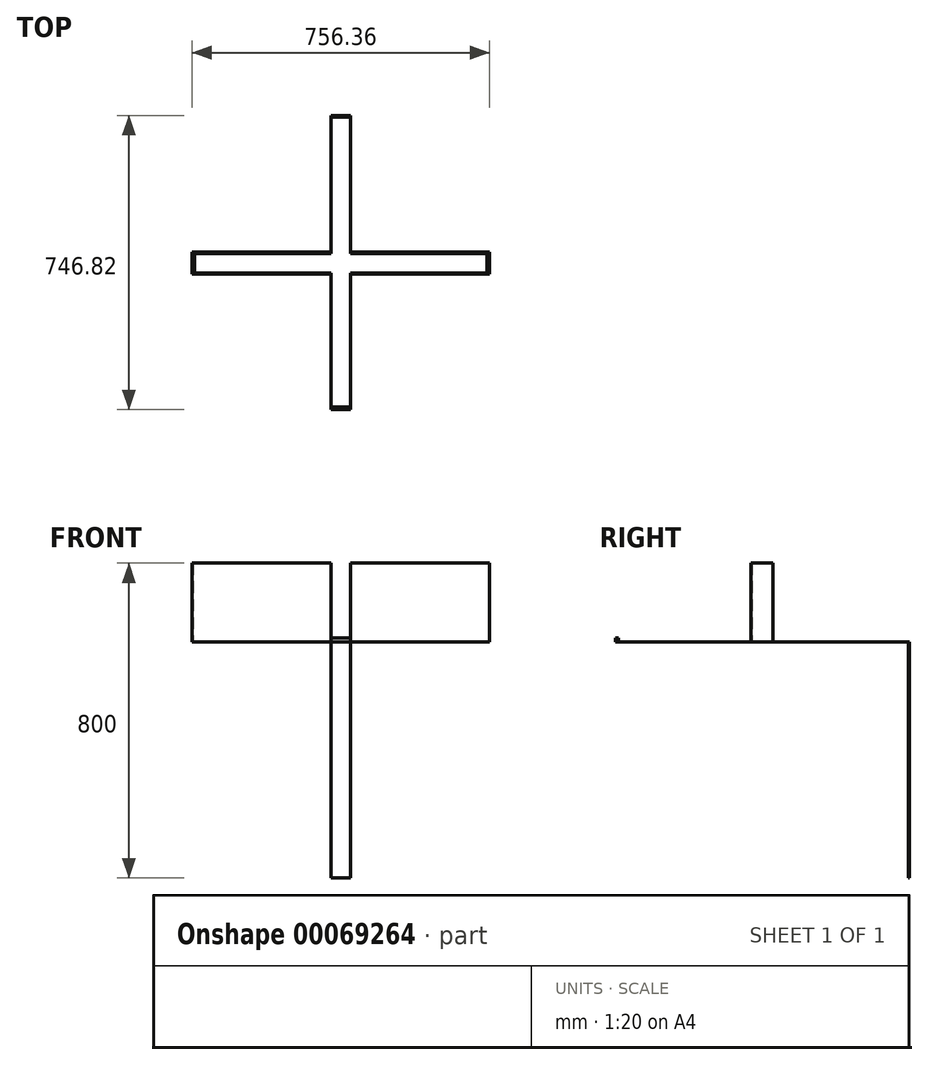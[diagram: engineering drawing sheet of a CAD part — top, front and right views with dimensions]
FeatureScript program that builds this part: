
annotation { "Feature Type Name" : "Feature", "Feature Type Description" : "" }
export const myFeature = defineFeature(function(context is Context, id is Id, definition is map)
    precondition{}
    {
        {
            var Q0;
            Q0=qCreatedBy(makeId("Top.planeOp"),FACE);
            var sketch = newSketch(context, id + "F0", { "sketchPlane" : qUnion([Q0])});
            skLineSegment(sketch, "E0.rect.bottom", {"start": v(375, 25) * mm, "end": v(-375, 25) * mm});
            skLineSegment(sketch, "E0.rect.top", {"start": v(375, -25) * mm, "end": v(-375, -25) * mm});
            skLineSegment(sketch, "E0.rect.left", {"start": v(375, 25) * mm, "end": v(375, -25) * mm});
            skLineSegment(sketch, "E0.rect.right", {"start": v(-375, 25) * mm, "end": v(-375, -25) * mm});
            skPoint(sketch, "E0.rect.middle", {"position": v(0, 0) * mm});
            skLineSegment(sketch, "E1.rect.bottom", {"start": v(-25, 375) * mm, "end": v(25, 375) * mm});
            skLineSegment(sketch, "E1.rect.top", {"start": v(-25, -375) * mm, "end": v(25, -375) * mm});
            skLineSegment(sketch, "E1.rect.left", {"start": v(-25, 375) * mm, "end": v(-25, -375) * mm});
            skLineSegment(sketch, "E1.rect.right", {"start": v(25, 375) * mm, "end": v(25, -375) * mm});
            skPoint(sketch, "E2", {"position": v(25, 25) * mm});
            skPoint(sketch, "E3", {"position": v(-25, 25) * mm});
            skPoint(sketch, "E4", {"position": v(-25, -25) * mm});
            skPoint(sketch, "E5", {"position": v(25, -25) * mm});
            skLineSegment(sketch, "E6", {"start": v(-25, -365) * mm, "end": v(25, -365) * mm});
            skLineSegment(sketch, "E7", {"start": v(25, -28.18) * mm, "end": v(378.18, -28.18) * mm});
            skLineSegment(sketch, "E8", {"start": v(378.18, -28.18) * mm, "end": v(378.18, 28.18) * mm});
            skLineSegment(sketch, "E9", {"start": v(378.18, 28.18) * mm, "end": v(25, 28.18) * mm});
            skLineSegment(sketch, "E10", {"start": v(-25, 28.18) * mm, "end": v(-378.18, 28.18) * mm});
            skLineSegment(sketch, "E11", {"start": v(-378.18, 28.18) * mm, "end": v(-378.18, -28.18) * mm});
            skLineSegment(sketch, "E12", {"start": v(-378.18, -28.18) * mm, "end": v(-25, -28.18) * mm});
            skLineSegment(sketch, "E13.bottom", {"start": v(375, 25) * mm, "end": v(371.83, 25) * mm});
            skLineSegment(sketch, "E13.top", {"start": v(375, -25) * mm, "end": v(371.83, -25) * mm});
            skLineSegment(sketch, "E13.right", {"start": v(371.83, 25) * mm, "end": v(371.83, -25) * mm});
            skLineSegment(sketch, "E14.bottom", {"start": v(25, -375) * mm, "end": v(-25, -375) * mm});
            skLineSegment(sketch, "E14.top", {"start": v(25, -371.83) * mm, "end": v(-25, -371.83) * mm});
            skLineSegment(sketch, "E14.left", {"start": v(25, -375) * mm, "end": v(25, -371.83) * mm});
            skLineSegment(sketch, "E14.right", {"start": v(-25, -375) * mm, "end": v(-25, -371.83) * mm});
            skLineSegment(sketch, "E15.bottom", {"start": v(-375, 25) * mm, "end": v(-371.83, 25) * mm});
            skLineSegment(sketch, "E15.top", {"start": v(-375, -25) * mm, "end": v(-371.83, -25) * mm});
            skLineSegment(sketch, "E15.right", {"start": v(-371.83, 25) * mm, "end": v(-371.83, -25) * mm});
            skLineSegment(sketch, "E16.top", {"start": v(-25, 371.83) * mm, "end": v(25, 371.83) * mm});
            skLineSegment(sketch, "E16.left", {"start": v(-25, 375) * mm, "end": v(-25, 371.83) * mm});
            skLineSegment(sketch, "E16.right", {"start": v(25, 375) * mm, "end": v(25, 371.83) * mm});
            skLineSegment(sketch, "E17.bottom", {"start": v(-21.82, -21.82) * mm, "end": v(21.82, -21.82) * mm});
            skLineSegment(sketch, "E17.top", {"start": v(-21.83, 21.82) * mm, "end": v(21.82, 21.83) * mm});
            skLineSegment(sketch, "E17.left", {"start": v(-21.82, -21.82) * mm, "end": v(-21.83, 21.82) * mm});
            skLineSegment(sketch, "E17.right", {"start": v(21.82, -21.82) * mm, "end": v(21.82, 21.83) * mm});
            skSolve(sketch);
        }
        {
            var Q0;
            {var subQ8=sQuery(id+"F0.wireOp",EDGE,"E10");Q0=makeQuery(id+"F0.imprint","IMPRINT",FACE,{"disambiguationData":[TD([[makeQuery(id+"F0.imprint","IMPRINT",EDGE,{"derivedFrom":subQ8}),1.0]])]});}
            var Q1;
            {var subQ0=sQuery(id+"F0.wireOp",EDGE,"E7");Q1=makeQuery(id+"F0.imprint","IMPRINT",FACE,{"disambiguationData":[TD([[makeQuery(id+"F0.imprint","IMPRINT",EDGE,{"derivedFrom":subQ0}),1.0]])]});}
            extrude(context, id + "F1", {"entities" : qUnion([Q0, Q1]), "depth" : 200 * mm});
        }
        {
            var Q0;
            Q0=makeQuery(id+"F0.imprint","IMPRINT",FACE,{"disambiguationData":[TD([[makeQuery(id+"F0.imprint","IMPRINT",EDGE,{"derivedFrom":sQuery(id+"F0.wireOp",EDGE,"E17.bottom")}),-1.0]])]});
            var Q1;
            {var subQ4=sQuery(id+"F0.wireOp",EDGE,"E6");Q1=makeQuery(id+"F0.imprint","IMPRINT",FACE,{"disambiguationData":[TD([[makeQuery(id+"F0.imprint","IMPRINT",EDGE,{"derivedFrom":subQ4}),1.0]])]});}
            var Q2;
            {var subQ2=sQuery(id+"F0.wireOp",EDGE,"E6");Q2=makeQuery(id+"F0.imprint","IMPRINT",FACE,{"disambiguationData":[TD([[makeQuery(id+"F0.imprint","IMPRINT",EDGE,{"derivedFrom":subQ2}),-1.0]])]});}
            var Q3;
            {var subQ0=sQuery(id+"F0.wireOp",EDGE,"E15.right");Q3=makeQuery(id+"F0.imprint","IMPRINT",FACE,{"disambiguationData":[TD([[makeQuery(id+"F0.imprint","IMPRINT",EDGE,{"derivedFrom":subQ0}),1.0]])]});}
            var Q4;
            Q4=makeQuery(id+"F0.imprint","IMPRINT",FACE,{"disambiguationData":[TD([[makeQuery(id+"F0.imprint","IMPRINT",EDGE,{"derivedFrom":sQuery(id+"F0.wireOp",EDGE,"E17.bottom")}),1.0]])]});
            var Q5;
            {var subQ0=sQuery(id+"F0.wireOp",EDGE,"E13.right");Q5=makeQuery(id+"F0.imprint","IMPRINT",FACE,{"disambiguationData":[TD([[makeQuery(id+"F0.imprint","IMPRINT",EDGE,{"derivedFrom":subQ0}),-1.0]])]});}
            var Q6;
            {var subQ0=sQuery(id+"F0.wireOp",EDGE,"E16.top");Q6=makeQuery(id+"F0.imprint","IMPRINT",FACE,{"disambiguationData":[TD([[makeQuery(id+"F0.imprint","IMPRINT",EDGE,{"derivedFrom":subQ0}),-1.0]])]});}
            var Q7;
            Q7=makeQuery(id+"F0.imprint","IMPRINT",FACE,{"disambiguationData":[TD([[makeQuery(id+"F0.imprint","IMPRINT",EDGE,{"derivedFrom":sQuery(id+"F0.wireOp",EDGE,"E15.bottom")}),-1.0]])]});
            var Q8;
            Q8=makeQuery(id+"F0.imprint","IMPRINT",FACE,{"disambiguationData":[TD([[makeQuery(id+"F0.imprint","IMPRINT",EDGE,{"derivedFrom":sQuery(id+"F0.wireOp",EDGE,"E13.bottom")}),1.0]])]});
            var Q9;
            Q9=makeQuery(id+"F0.imprint","IMPRINT",FACE,{"disambiguationData":[TD([[makeQuery(id+"F0.imprint","IMPRINT",EDGE,{"derivedFrom":sQuery(id+"F0.wireOp",EDGE,"E1.rect.bottom")}),-1.0]])]});
            var Q10;
            Q10=makeQuery(id+"F0.imprint","IMPRINT",FACE,{"disambiguationData":[TD([[makeQuery(id+"F0.imprint","IMPRINT",EDGE,{"derivedFrom":sQuery(id+"F0.wireOp",EDGE,"E14.bottom")}),-1.0]])]});
            extrude(context, id + "F2", {"entities" : qUnion([Q0, Q1, Q2, Q3, Q4, Q5, Q6, Q7, Q8, Q9, Q10]), "depth" : 1 / 203.2 * mm});
        }
        {
            var Q0;
            Q0=makeQuery(id+"F2.opExtrude","CAP_FACE",FACE,{"disambiguationData":[OSD([sQuery(id+"F0.wireOp",EDGE,"E0.rect.bottom"),sQuery(id+"F0.wireOp",EDGE,"E0.rect.top"),sQuery(id+"F0.wireOp",EDGE,"E0.rect.left"),sQuery(id+"F0.wireOp",EDGE,"E0.rect.right"),sQuery(id+"F0.wireOp",EDGE,"E1.rect.bottom"),sQuery(id+"F0.wireOp",EDGE,"E1.rect.top"),sQuery(id+"F0.wireOp",EDGE,"E1.rect.left"),sQuery(id+"F0.wireOp",EDGE,"E1.rect.right")])],"isStart":false});
            var sketch = newSketch(context, id + "F3", { "sketchPlane" : qUnion([Q0])});
            skLineSegment(sketch, "E18.0", {"start": v(-25, -365) * mm, "end": v(25, -365) * mm});
            skSolve(sketch);
        }
        {
            var Q0;
            {var subQ0=sQuery(id+"F3.wireOp",EDGE,"E18.0");Q0=makeQuery(id+"F3.imprint","IMPRINT",FACE,{"disambiguationData":[TD([[makeQuery(id+"F3.imprint","IMPRINT",EDGE,{"derivedFrom":subQ0}),-1.0]])]});}
            extrude(context, id + "F4", {"entities" : qUnion([Q0]), "depth" : 10 * mm});
        }
        {
            var Q0;
            Q0=makeQuery(id+"F0.imprint","IMPRINT",FACE,{"disambiguationData":[TD([[makeQuery(id+"F0.imprint","IMPRINT",EDGE,{"derivedFrom":sQuery(id+"F0.wireOp",EDGE,"E1.rect.bottom")}),-1.0]])]});
            var Q1;
            Q1=makeQuery(id+"F0.imprint","IMPRINT",FACE,{"disambiguationData":[TD([[makeQuery(id+"F0.imprint","IMPRINT",EDGE,{"derivedFrom":sQuery(id+"F0.wireOp",EDGE,"E15.bottom")}),-1.0]])]});
            var Q2;
            Q2=makeQuery(id+"F0.imprint","IMPRINT",FACE,{"disambiguationData":[TD([[makeQuery(id+"F0.imprint","IMPRINT",EDGE,{"derivedFrom":sQuery(id+"F0.wireOp",EDGE,"E13.bottom")}),1.0]])]});
            var Q3;
            Q3=makeQuery(id+"F0.imprint","IMPRINT",FACE,{"disambiguationData":[TD([[makeQuery(id+"F0.imprint","IMPRINT",EDGE,{"derivedFrom":sQuery(id+"F0.wireOp",EDGE,"E14.bottom")}),-1.0]])]});
            extrude(context, id + "F5", {"entities" : qUnion([Q0, Q1, Q2, Q3]), "oppositeDirection" : true, "depth" : 600 * mm});
        }
    });
